# Revit family: Maxlogic Газовый приемно-контрольный прибор,  8 шлейфов, 16 релейных выходов
name_source: partatom
category: Fire Alarm Devices
units: mm (PartAtom-declared; Revit-internal decimal feet)

## family parameters
Cut with Voids When Loaded = No
Host = Face
Maintain Annotation Orientation = Yes
OmniClass Number = 23.85.30.21
OmniClass Title = Environmental Detection/Registration
Part Type = Normal
Room Calculation Point = No
Round Connector Dimension = Use Diameter
Shared = No

## types (1)
- Maxlogic Газовый приемно-контрольный прибор,  8 шлейфов, 16 релейных выходов
    Cost = 0 $
    Default Elevation = 0 mm  [stored 0 ft]
    Description = Газовый приемно-контрольный прибор,  8 шлейфов, 16 релейных выходов
    Manufacturer = Mavili Elektronik Ticaret A.Ş.
    Model = Maxlogic
    URL = https://www.mavili.com.tr
    Адрес №1 = Şerifali Mahallesi Kutup Sokak No:27/1-2-4 Ümraniye TR-34775 İSTANBUL
    Аккумулятор = 2 X ( (12В Пост. ток 7 Aм/ч. )
    Вес = 5500 гр
    Вторичный материал = Белый пластмассовый ABS
    Гарантийный срок = Года
    Гарантийный срок запчастей = 2
    Гарантия срока службы = 2
    Главный Материал = Серый металлический
    Инструкция по установке = https://mavilielektronik.com
    Код продукта = ML-4218
    Монтажная поверхность = Настенная
    Номер телефона = (+)90 216 466 45 05
    Номер факса = (+)90 216 466 45 10
    Номинальная высота = 300 мм
    Номинальная глубина = 100 мм
    Номинальная ширина = 400 мм
    Производительность кода = EN 54-2, EN 54-4
    Рабочая Температура = (-10°C) - (+55°C)
    Резервное питание = 220 В Перем. ток
    Цвет = Белый

note: [stored X ft] marks values corroborated as IEEE doubles in the binary element streams (Revit-internal decimal feet)

## geometry (parser evidence)
native form markers: Sweep x2
no freeform markers — native parametric forms only
